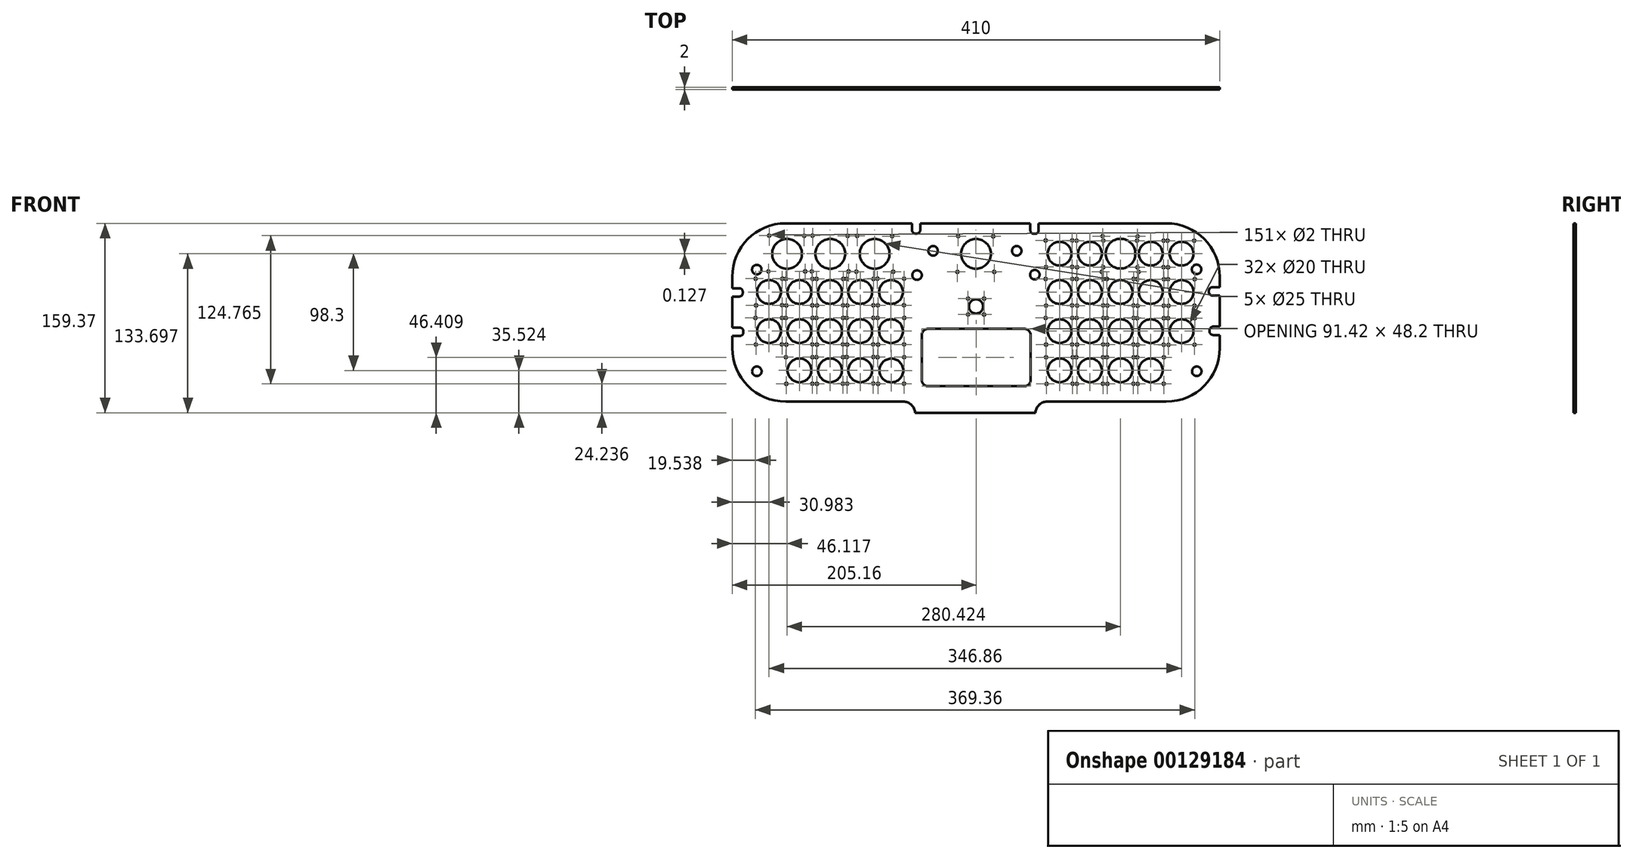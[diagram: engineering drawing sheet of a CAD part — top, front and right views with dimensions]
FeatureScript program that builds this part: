
annotation { "Feature Type Name" : "Feature", "Feature Type Description" : "" }
export const myFeature = defineFeature(function(context is Context, id is Id, definition is map)
    precondition{}
    {
        {
            var Q0;
            Q0=qCreatedBy(makeId("Front.planeOp"),FACE);
            var sketch = newSketch(context, id + "F0", { "sketchPlane" : qUnion([Q0])});
            skLineSegment(sketch, "E0.bottom", {"start": v(205, -75) * mm, "end": v(-205, -75) * mm});
            skLineSegment(sketch, "E0.top", {"start": v(205, 75) * mm, "end": v(-205, 75) * mm});
            skLineSegment(sketch, "E0.left", {"start": v(205, -75) * mm, "end": v(205, 75) * mm});
            skLineSegment(sketch, "E0.right", {"start": v(-205, -75) * mm, "end": v(-205, 75) * mm});
            skSolve(sketch);
        }
        {
            var Q0;
            Q0=qSketchRegion(id+"F0",true);
            extrude(context, id + "F1", {"entities" : qUnion([Q0]), "depth" : 1 * mm, "hasSecondDirection" : true, "secondDirectionOppositeDirection" : true, "secondDirectionDepth" : 1 * mm});
        }
        {
            var Q0;
            Q0=makeQuery(id+"F1.opExtrude","SWEPT_EDGE",EDGE,{"disambiguationData":[OSD([sQuery(id+"F0.wireOp",EDGE,"E0.top"),sQuery(id+"F0.wireOp",EDGE,"E0.right")])]});
            var Q1;
            Q1=makeQuery(id+"F1.opExtrude","SWEPT_EDGE",EDGE,{"disambiguationData":[OSD([sQuery(id+"F0.wireOp",EDGE,"E0.bottom"),sQuery(id+"F0.wireOp",EDGE,"E0.right")])]});
            fillet(context, id + "F2", {"entities" : qUnion([Q0, Q1]), "radius" : 45 * mm, "tangentPropagation" : true, "allowEdgeOverflow" : false});
        }
        {
            var Q0;
            Q0=makeQuery(id+"F1.opExtrude","SWEPT_EDGE",EDGE,{"disambiguationData":[OSD([sQuery(id+"F0.wireOp",EDGE,"E0.top"),sQuery(id+"F0.wireOp",EDGE,"E0.left")])]});
            fillet(context, id + "F3", {"entities" : qUnion([Q0]), "radius" : 45 * mm, "tangentPropagation" : true, "allowEdgeOverflow" : false});
        }
        {
            var Q0;
            Q0=makeQuery(id+"F1.opExtrude","SWEPT_EDGE",EDGE,{"disambiguationData":[OSD([sQuery(id+"F0.wireOp",EDGE,"E0.bottom"),sQuery(id+"F0.wireOp",EDGE,"E0.left")])]});
            fillet(context, id + "F4", {"entities" : qUnion([Q0]), "radius" : 45 * mm, "tangentPropagation" : true, "allowEdgeOverflow" : false});
        }
        {
            var Q0;
            Q0=qCreatedBy(makeId("Front.planeOp"),FACE);
            var sketch = newSketch(context, id + "F5", { "sketchPlane" : qUnion([Q0])});
            skLineSegment(sketch, "E1.bottom", {"start": v(-51.28, -63.48) * mm, "end": v(50, -63.48) * mm});
            skLineSegment(sketch, "E1.top", {"start": v(-51.28, -84.37) * mm, "end": v(50, -84.37) * mm});
            skLineSegment(sketch, "E1.left", {"start": v(-51.28, -63.48) * mm, "end": v(-51.28, -84.37) * mm});
            skLineSegment(sketch, "E1.right", {"start": v(50, -63.48) * mm, "end": v(50, -84.37) * mm});
            skSolve(sketch);
        }
        {
            var Q0;
            Q0=qSketchRegion(id+"F5",true);
            extrude(context, id + "F6", {"entities" : qUnion([Q0]), "operationType" : NewBodyOperationType.ADD, "depth" : 1 * mm, "hasSecondDirection" : true, "secondDirectionOppositeDirection" : true, "secondDirectionDepth" : 1 * mm});
        }
        {
            var Q0;
            Q0=makeQuery(id+"F6.boolean.opBoolean","INTERSECT",EDGE,{"derivedFrom":[makeQuery(id+"F1.opExtrude","SWEPT_FACE",FACE,{"disambiguationData":[OSD([sQuery(id+"F0.wireOp",EDGE,"E0.bottom")])]}),makeQuery(id+"F6.opExtrude","SWEPT_FACE",FACE,{"disambiguationData":[OSD([sQuery(id+"F5.wireOp",EDGE,"E1.left")])]})]});
            fillet(context, id + "F7", {"entities" : qUnion([Q0]), "radius" : 10 * mm, "tangentPropagation" : true, "allowEdgeOverflow" : false});
        }
        {
            var Q0;
            Q0=makeQuery(id+"F6.boolean.opBoolean","INTERSECT",EDGE,{"derivedFrom":[makeQuery(id+"F1.opExtrude","SWEPT_FACE",FACE,{"disambiguationData":[OSD([sQuery(id+"F0.wireOp",EDGE,"E0.bottom")])]}),makeQuery(id+"F6.opExtrude","SWEPT_FACE",FACE,{"disambiguationData":[OSD([sQuery(id+"F5.wireOp",EDGE,"E1.right")])]})]});
            fillet(context, id + "F8", {"entities" : qUnion([Q0]), "radius" : 10 * mm, "tangentPropagation" : true, "allowEdgeOverflow" : false});
        }
        {
            var Q0;
            Q0=qCreatedBy(makeId("Front.planeOp"),FACE);
            var sketch = newSketch(context, id + "F9", { "sketchPlane" : qUnion([Q0])});
            skCircle(sketch, "E2", {"center": v(0, 49.33) * mm, "radius": 12.5 * mm});
            skCircle(sketch, "E3", {"center": v(0, 5.03) * mm, "radius": 6 * mm});
            skCircle(sketch, "E4", {"center": v(-158.88, 49.33) * mm, "radius": 12.5 * mm});
            skCircle(sketch, "E5", {"center": v(-122.54, 49.33) * mm, "radius": 12.5 * mm});
            skCircle(sketch, "E6", {"center": v(-85.24, 49.33) * mm, "radius": 12.5 * mm});
            skCircle(sketch, "E7", {"center": v(172.84, 17.2) * mm, "radius": 10 * mm});
            skCircle(sketch, "E8", {"center": v(172.84, -15.76) * mm, "radius": 10 * mm});
            skCircle(sketch, "E9", {"center": v(146.94, -48.73) * mm, "radius": 10 * mm});
            skCircle(sketch, "E10", {"center": v(146.94, 17.2) * mm, "radius": 10 * mm});
            skCircle(sketch, "E11", {"center": v(146.94, -15.76) * mm, "radius": 10 * mm});
            skCircle(sketch, "E12", {"center": v(121.54, -48.73) * mm, "radius": 10 * mm});
            skCircle(sketch, "E13", {"center": v(121.54, 17.2) * mm, "radius": 10 * mm});
            skCircle(sketch, "E14", {"center": v(121.54, -15.76) * mm, "radius": 10 * mm});
            skCircle(sketch, "E15", {"center": v(95.83, -48.73) * mm, "radius": 10 * mm});
            skCircle(sketch, "E16", {"center": v(95.83, 17.2) * mm, "radius": 10 * mm});
            skCircle(sketch, "E17", {"center": v(95.83, -15.76) * mm, "radius": 10 * mm});
            skCircle(sketch, "E18", {"center": v(70.27, -48.73) * mm, "radius": 10 * mm});
            skCircle(sketch, "E19", {"center": v(70.27, 17.2) * mm, "radius": 10 * mm});
            skCircle(sketch, "E20", {"center": v(70.27, -15.76) * mm, "radius": 10 * mm});
            skCircle(sketch, "E21", {"center": v(172.84, 49.45) * mm, "radius": 10 * mm});
            skCircle(sketch, "E22", {"center": v(146.94, 49.45) * mm, "radius": 10 * mm});
            skCircle(sketch, "E23", {"center": v(121.54, 49.45) * mm, "radius": 12.5 * mm});
            skCircle(sketch, "E24", {"center": v(95.83, 49.45) * mm, "radius": 10 * mm});
            skCircle(sketch, "E25", {"center": v(70.27, 49.45) * mm, "radius": 10 * mm});
            skCircle(sketch, "E26", {"center": v(-71.45, 17.2) * mm, "radius": 10 * mm});
            skCircle(sketch, "E27", {"center": v(-71.45, -15.76) * mm, "radius": 10 * mm});
            skCircle(sketch, "E28", {"center": v(-97.35, -48.73) * mm, "radius": 10 * mm});
            skCircle(sketch, "E29", {"center": v(-97.35, 17.2) * mm, "radius": 10 * mm});
            skCircle(sketch, "E30", {"center": v(-97.35, -15.76) * mm, "radius": 10 * mm});
            skCircle(sketch, "E31", {"center": v(-122.75, -48.73) * mm, "radius": 10 * mm});
            skCircle(sketch, "E32", {"center": v(-122.75, 17.2) * mm, "radius": 10 * mm});
            skCircle(sketch, "E33", {"center": v(-122.75, -15.76) * mm, "radius": 10 * mm});
            skCircle(sketch, "E34", {"center": v(-148.46, -48.73) * mm, "radius": 10 * mm});
            skCircle(sketch, "E35", {"center": v(-148.46, 17.2) * mm, "radius": 10 * mm});
            skCircle(sketch, "E36", {"center": v(-148.46, -15.76) * mm, "radius": 10 * mm});
            skCircle(sketch, "E37", {"center": v(-174.02, 17.2) * mm, "radius": 10 * mm});
            skCircle(sketch, "E38", {"center": v(-174.02, -15.76) * mm, "radius": 10 * mm});
            skCircle(sketch, "E39", {"center": v(-71.2, -48.85) * mm, "radius": 10 * mm});
            skLineSegment(sketch, "E40.bottom", {"start": v(-45.55, -13.86) * mm, "end": v(45.87, -13.86) * mm});
            skLineSegment(sketch, "E40.top", {"start": v(-45.55, -62.06) * mm, "end": v(45.87, -62.06) * mm});
            skLineSegment(sketch, "E40.left", {"start": v(-45.55, -13.86) * mm, "end": v(-45.55, -62.06) * mm});
            skLineSegment(sketch, "E40.right", {"start": v(45.87, -13.86) * mm, "end": v(45.87, -62.06) * mm});
            skSolve(sketch);
        }
        {
            var Q0;
            Q0=makeQuery(id+"F6.boolean.opBoolean","MERGE",FACE,{"derivedFrom":[makeQuery(id+"F1.opExtrude","CAP_FACE",FACE,{"disambiguationData":[OSD([sQuery(id+"F0.wireOp",EDGE,"E0.bottom"),sQuery(id+"F0.wireOp",EDGE,"E0.top"),sQuery(id+"F0.wireOp",EDGE,"E0.left"),sQuery(id+"F0.wireOp",EDGE,"E0.right")])],"isStart":false}),makeQuery(id+"F6.opExtrude","CAP_FACE",FACE,{"disambiguationData":[OSD([sQuery(id+"F5.wireOp",EDGE,"E1.bottom"),sQuery(id+"F5.wireOp",EDGE,"E1.top"),sQuery(id+"F5.wireOp",EDGE,"E1.left"),sQuery(id+"F5.wireOp",EDGE,"E1.right")])],"isStart":false})]});
            cPlane(context, id + "F10", {"entities" : qUnion([Q0]), "cplaneType" : CPlaneType.OFFSET, "offset" : 0 * mm, "width" : 150 * mm, "height" : 150 * mm});
        }
        {
            var Q0;
            Q0=qCreatedBy(id+"F10.planeOp",FACE);
            var sketch = newSketch(context, id + "F11", { "sketchPlane" : qUnion([Q0])});
            skLineSegment(sketch, "E41.bottom", {"start": v(-210.38, 20.36) * mm, "end": v(-199.13, 20.36) * mm});
            skLineSegment(sketch, "E41.top", {"start": v(-210.38, 13.36) * mm, "end": v(-199.13, 13.36) * mm});
            skLineSegment(sketch, "E41.left", {"start": v(-213.38, 17.36) * mm, "end": v(-213.38, 16.36) * mm});
            skLineSegment(sketch, "E41.right", {"start": v(-196.13, 17.36) * mm, "end": v(-196.13, 16.36) * mm});
            skPoint(sketch, "E42.visualSharp", {"position": v(-196.13, 20.36) * mm});
            skArc(sketch, "E42.filletArc", {"start": v(-196.13, 17.36) * mm, "mid": v(-197.01, 19.48) * mm, "end": v(-199.13, 20.36) * mm});
            skPoint(sketch, "E43.visualSharp", {"position": v(-196.13, 13.36) * mm});
            skArc(sketch, "E43.filletArc", {"start": v(-199.13, 13.36) * mm, "mid": v(-197.01, 14.23) * mm, "end": v(-196.13, 16.36) * mm});
            skPoint(sketch, "E44.visualSharp", {"position": v(-213.38, 20.36) * mm});
            skArc(sketch, "E44.filletArc", {"start": v(-210.38, 20.36) * mm, "mid": v(-212.5, 19.48) * mm, "end": v(-213.38, 17.36) * mm});
            skPoint(sketch, "E45.visualSharp", {"position": v(-213.38, 13.36) * mm});
            skArc(sketch, "E45.filletArc", {"start": v(-213.38, 16.36) * mm, "mid": v(-212.5, 14.23) * mm, "end": v(-210.38, 13.36) * mm});
            skLineSegment(sketch, "E46.bottom", {"start": v(-209.84, -12.8) * mm, "end": v(-198.59, -12.8) * mm});
            skLineSegment(sketch, "E46.top", {"start": v(-209.84, -19.8) * mm, "end": v(-198.59, -19.8) * mm});
            skLineSegment(sketch, "E46.left", {"start": v(-212.84, -15.8) * mm, "end": v(-212.84, -16.8) * mm});
            skLineSegment(sketch, "E46.right", {"start": v(-195.59, -15.8) * mm, "end": v(-195.59, -16.8) * mm});
            skPoint(sketch, "E47.visualSharp", {"position": v(-195.59, -12.8) * mm});
            skArc(sketch, "E47.filletArc", {"start": v(-195.59, -15.8) * mm, "mid": v(-196.47, -13.69) * mm, "end": v(-198.59, -12.8) * mm});
            skPoint(sketch, "E48.visualSharp", {"position": v(-195.59, -19.8) * mm});
            skArc(sketch, "E48.filletArc", {"start": v(-198.59, -19.8) * mm, "mid": v(-196.47, -18.93) * mm, "end": v(-195.59, -16.8) * mm});
            skPoint(sketch, "E49.visualSharp", {"position": v(-212.84, -12.8) * mm});
            skArc(sketch, "E49.filletArc", {"start": v(-209.84, -12.8) * mm, "mid": v(-211.96, -13.69) * mm, "end": v(-212.84, -15.8) * mm});
            skPoint(sketch, "E50.visualSharp", {"position": v(-212.84, -19.8) * mm});
            skArc(sketch, "E50.filletArc", {"start": v(-212.84, -16.8) * mm, "mid": v(-211.96, -18.93) * mm, "end": v(-209.84, -19.8) * mm});
            skLineSegment(sketch, "E51.bottom", {"start": v(198.82, 21.2) * mm, "end": v(210.07, 21.2) * mm});
            skLineSegment(sketch, "E51.top", {"start": v(198.82, 14.2) * mm, "end": v(210.07, 14.2) * mm});
            skLineSegment(sketch, "E51.left", {"start": v(195.82, 18.2) * mm, "end": v(195.82, 17.2) * mm});
            skLineSegment(sketch, "E51.right", {"start": v(213.07, 18.2) * mm, "end": v(213.07, 17.2) * mm});
            skPoint(sketch, "E52.visualSharp", {"position": v(213.07, 21.2) * mm});
            skArc(sketch, "E52.filletArc", {"start": v(213.07, 18.2) * mm, "mid": v(212.2, 20.32) * mm, "end": v(210.07, 21.2) * mm});
            skPoint(sketch, "E53.visualSharp", {"position": v(213.07, 14.2) * mm});
            skArc(sketch, "E53.filletArc", {"start": v(210.07, 14.2) * mm, "mid": v(212.2, 15.07) * mm, "end": v(213.07, 17.2) * mm});
            skPoint(sketch, "E54.visualSharp", {"position": v(195.82, 21.2) * mm});
            skArc(sketch, "E54.filletArc", {"start": v(198.82, 21.2) * mm, "mid": v(196.7, 20.32) * mm, "end": v(195.82, 18.2) * mm});
            skPoint(sketch, "E55.visualSharp", {"position": v(195.82, 14.2) * mm});
            skArc(sketch, "E55.filletArc", {"start": v(195.82, 17.2) * mm, "mid": v(196.7, 15.07) * mm, "end": v(198.82, 14.2) * mm});
            skLineSegment(sketch, "E56.bottom", {"start": v(199.36, -11.97) * mm, "end": v(210.61, -11.97) * mm});
            skLineSegment(sketch, "E56.top", {"start": v(199.36, -18.97) * mm, "end": v(210.61, -18.97) * mm});
            skLineSegment(sketch, "E56.left", {"start": v(196.36, -14.97) * mm, "end": v(196.36, -15.97) * mm});
            skLineSegment(sketch, "E56.right", {"start": v(213.61, -14.97) * mm, "end": v(213.61, -15.97) * mm});
            skPoint(sketch, "E57.visualSharp", {"position": v(213.61, -11.97) * mm});
            skArc(sketch, "E57.filletArc", {"start": v(213.61, -14.97) * mm, "mid": v(212.73, -12.85) * mm, "end": v(210.61, -11.97) * mm});
            skPoint(sketch, "E58.visualSharp", {"position": v(213.61, -18.97) * mm});
            skArc(sketch, "E58.filletArc", {"start": v(210.61, -18.97) * mm, "mid": v(212.73, -18.1) * mm, "end": v(213.61, -15.97) * mm});
            skPoint(sketch, "E59.visualSharp", {"position": v(196.36, -11.97) * mm});
            skArc(sketch, "E59.filletArc", {"start": v(199.36, -11.97) * mm, "mid": v(197.24, -12.85) * mm, "end": v(196.36, -14.97) * mm});
            skPoint(sketch, "E60.visualSharp", {"position": v(196.36, -18.97) * mm});
            skArc(sketch, "E60.filletArc", {"start": v(196.36, -15.97) * mm, "mid": v(197.24, -18.1) * mm, "end": v(199.36, -18.97) * mm});
            skLineSegment(sketch, "E61.bottom", {"start": v(-50.84, 85.12) * mm, "end": v(-49.84, 85.12) * mm});
            skLineSegment(sketch, "E61.top", {"start": v(-50.84, 66.34) * mm, "end": v(-49.84, 66.34) * mm});
            skLineSegment(sketch, "E61.left", {"start": v(-53.84, 82.12) * mm, "end": v(-53.84, 69.34) * mm});
            skLineSegment(sketch, "E61.right", {"start": v(-46.84, 82.12) * mm, "end": v(-46.84, 69.34) * mm});
            skPoint(sketch, "E62.visualSharp", {"position": v(-53.84, 85.12) * mm});
            skArc(sketch, "E62.filletArc", {"start": v(-50.84, 85.12) * mm, "mid": v(-52.96, 84.24) * mm, "end": v(-53.84, 82.12) * mm});
            skPoint(sketch, "E63.visualSharp", {"position": v(-46.84, 85.12) * mm});
            skArc(sketch, "E63.filletArc", {"start": v(-46.84, 82.12) * mm, "mid": v(-47.72, 84.24) * mm, "end": v(-49.84, 85.12) * mm});
            skPoint(sketch, "E64.visualSharp", {"position": v(-46.84, 66.34) * mm});
            skArc(sketch, "E64.filletArc", {"start": v(-49.84, 66.34) * mm, "mid": v(-47.72, 67.22) * mm, "end": v(-46.84, 69.34) * mm});
            skPoint(sketch, "E65.visualSharp", {"position": v(-53.84, 66.34) * mm});
            skArc(sketch, "E65.filletArc", {"start": v(-53.84, 69.34) * mm, "mid": v(-52.96, 67.22) * mm, "end": v(-50.84, 66.34) * mm});
            skLineSegment(sketch, "E66.bottom", {"start": v(48.7, 84.97) * mm, "end": v(49.7, 84.97) * mm});
            skLineSegment(sketch, "E66.top", {"start": v(48.7, 66.19) * mm, "end": v(49.7, 66.19) * mm});
            skLineSegment(sketch, "E66.left", {"start": v(45.7, 81.97) * mm, "end": v(45.7, 69.19) * mm});
            skLineSegment(sketch, "E66.right", {"start": v(52.7, 81.97) * mm, "end": v(52.7, 69.19) * mm});
            skPoint(sketch, "E67.visualSharp", {"position": v(45.7, 84.97) * mm});
            skArc(sketch, "E67.filletArc", {"start": v(48.7, 84.97) * mm, "mid": v(46.57, 84.09) * mm, "end": v(45.7, 81.97) * mm});
            skPoint(sketch, "E68.visualSharp", {"position": v(52.7, 84.97) * mm});
            skArc(sketch, "E68.filletArc", {"start": v(52.7, 81.97) * mm, "mid": v(51.81, 84.09) * mm, "end": v(49.7, 84.97) * mm});
            skPoint(sketch, "E69.visualSharp", {"position": v(52.7, 66.19) * mm});
            skArc(sketch, "E69.filletArc", {"start": v(49.7, 66.19) * mm, "mid": v(51.81, 67.07) * mm, "end": v(52.7, 69.19) * mm});
            skPoint(sketch, "E70.visualSharp", {"position": v(45.7, 66.19) * mm});
            skArc(sketch, "E70.filletArc", {"start": v(45.7, 69.19) * mm, "mid": v(46.57, 67.07) * mm, "end": v(48.7, 66.19) * mm});
            skSolve(sketch);
        }
        {
            var Q0;
            Q0=makeQuery(id+"F6.boolean.opBoolean","MERGE",FACE,{"derivedFrom":[makeQuery(id+"F1.opExtrude","CAP_FACE",FACE,{"disambiguationData":[OSD([sQuery(id+"F0.wireOp",EDGE,"E0.bottom"),sQuery(id+"F0.wireOp",EDGE,"E0.top"),sQuery(id+"F0.wireOp",EDGE,"E0.left"),sQuery(id+"F0.wireOp",EDGE,"E0.right")])],"isStart":false}),makeQuery(id+"F6.opExtrude","CAP_FACE",FACE,{"disambiguationData":[OSD([sQuery(id+"F5.wireOp",EDGE,"E1.bottom"),sQuery(id+"F5.wireOp",EDGE,"E1.top"),sQuery(id+"F5.wireOp",EDGE,"E1.left"),sQuery(id+"F5.wireOp",EDGE,"E1.right")])],"isStart":false})]});
            cPlane(context, id + "F12", {"entities" : qUnion([Q0]), "cplaneType" : CPlaneType.OFFSET, "offset" : 2 * mm, "oppositeDirection" : true, "width" : 150 * mm, "height" : 150 * mm});
        }
        {
            var Q0;
            Q0=qCreatedBy(id+"F12.planeOp",FACE);
            var sketch = newSketch(context, id + "F13", { "sketchPlane" : qUnion([Q0])});
            skCircle(sketch, "E71", {"center": v(-184.3, 36.01) * mm, "radius": 4 * mm});
            skCircle(sketch, "E72", {"center": v(-184.28, -49.46) * mm, "radius": 4 * mm});
            skCircle(sketch, "E73", {"center": v(-36.07, 51.83) * mm, "radius": 4 * mm});
            skCircle(sketch, "E74", {"center": v(-49.57, 31.39) * mm, "radius": 4 * mm});
            skCircle(sketch, "E75", {"center": v(34.27, 51.83) * mm, "radius": 4 * mm});
            skCircle(sketch, "E76", {"center": v(49.46, 31.76) * mm, "radius": 4 * mm});
            skCircle(sketch, "E77", {"center": v(185.45, 36.26) * mm, "radius": 4 * mm});
            skCircle(sketch, "E78", {"center": v(185.64, -49.46) * mm, "radius": 4 * mm});
            skSolve(sketch);
        }
        {
            var Q0;
            Q0=qSketchRegion(id+"F13",true);
            extrude(context, id + "F14", {"entities" : qUnion([Q0]), "operationType" : NewBodyOperationType.REMOVE, "depth" : 28.49 * mm, "hasSecondDirection" : true, "secondDirectionOppositeDirection" : true, "secondDirectionDepth" : 25 * mm});
        }
        {
            var Q0;
            Q0 = qSketchRegion(id + "F9", true);
            extrude(context, id + "F15", {"entities" : qUnion([Q0]), "operationType" : NewBodyOperationType.REMOVE, "depth" : 25 * mm, "hasSecondDirection" : true, "secondDirectionOppositeDirection" : true, "secondDirectionDepth" : 25 * mm});
        }
        {
            var Q0;
            Q0 = qSketchRegion(id + "F11", true);
            extrude(context, id + "F16", {"entities" : qUnion([Q0]), "operationType" : NewBodyOperationType.REMOVE, "oppositeDirection" : true, "depth" : 50 * mm, "hasSecondDirection" : true, "secondDirectionOppositeDirection" : false, "secondDirectionDepth" : 50 * mm});
        }
        {
            var Q0;
            Q0=makeQuery(id+"F6.boolean.opBoolean","MERGE",FACE,{"derivedFrom":[makeQuery(id+"F1.opExtrude","CAP_FACE",FACE,{"disambiguationData":[OSD([sQuery(id+"F0.wireOp",EDGE,"E0.bottom"),sQuery(id+"F0.wireOp",EDGE,"E0.top"),sQuery(id+"F0.wireOp",EDGE,"E0.left"),sQuery(id+"F0.wireOp",EDGE,"E0.right")])],"isStart":true}),makeQuery(id+"F6.opExtrude","CAP_FACE",FACE,{"disambiguationData":[OSD([sQuery(id+"F5.wireOp",EDGE,"E1.bottom"),sQuery(id+"F5.wireOp",EDGE,"E1.top"),sQuery(id+"F5.wireOp",EDGE,"E1.left"),sQuery(id+"F5.wireOp",EDGE,"E1.right")])],"isStart":true})]});
            cPlane(context, id + "F17", {"entities" : qUnion([Q0]), "cplaneType" : CPlaneType.OFFSET, "offset" : 0 * mm, "oppositeDirection" : true, "width" : 150 * mm, "height" : 150 * mm});
        }
        {
            var Q0;
            Q0=qCreatedBy(id+"F17.planeOp",FACE);
            var sketch = newSketch(context, id + "F18", { "sketchPlane" : qUnion([Q0])});
            skLineSegment(sketch, "E79.bottom", {"start": v(184.07, 27.38) * mm, "end": v(163.8, 27.38) * mm, "construction": true});
            skLineSegment(sketch, "E79.top", {"start": v(184.07, 7.22) * mm, "end": v(163.8, 7.22) * mm, "construction": true});
            skLineSegment(sketch, "E79.left", {"start": v(184.07, 27.38) * mm, "end": v(184.07, 7.22) * mm, "construction": true});
            skLineSegment(sketch, "E79.right", {"start": v(163.8, 27.38) * mm, "end": v(163.8, 7.22) * mm, "construction": true});
            skPoint(sketch, "E80", {"position": v(185.32, 28.38) * mm});
            skPoint(sketch, "E81", {"position": v(162.91, 28.38) * mm});
            skPoint(sketch, "E82", {"position": v(184.95, 5.97) * mm});
            skPoint(sketch, "E83", {"position": v(163.04, 6.1) * mm});
            skLineSegment(sketch, "E84.bottom", {"start": v(158.64, 27.26) * mm, "end": v(138.36, 27.26) * mm, "construction": true});
            skLineSegment(sketch, "E84.top", {"start": v(158.64, 7.1) * mm, "end": v(138.36, 7.1) * mm, "construction": true});
            skLineSegment(sketch, "E84.left", {"start": v(158.64, 27.26) * mm, "end": v(158.64, 7.1) * mm, "construction": true});
            skLineSegment(sketch, "E84.right", {"start": v(138.36, 27.26) * mm, "end": v(138.36, 7.1) * mm, "construction": true});
            skPoint(sketch, "E85", {"position": v(159.89, 28.26) * mm});
            skPoint(sketch, "E86", {"position": v(137.48, 28.26) * mm});
            skPoint(sketch, "E87", {"position": v(159.51, 5.85) * mm});
            skPoint(sketch, "E88", {"position": v(137.6, 5.98) * mm});
            skLineSegment(sketch, "E89.bottom", {"start": v(132.78, 27.26) * mm, "end": v(112.5, 27.26) * mm, "construction": true});
            skLineSegment(sketch, "E89.top", {"start": v(132.78, 7.1) * mm, "end": v(112.5, 7.1) * mm, "construction": true});
            skLineSegment(sketch, "E89.left", {"start": v(132.78, 27.26) * mm, "end": v(132.78, 7.1) * mm, "construction": true});
            skLineSegment(sketch, "E89.right", {"start": v(112.5, 27.26) * mm, "end": v(112.5, 7.1) * mm, "construction": true});
            skPoint(sketch, "E90", {"position": v(134.03, 28.26) * mm});
            skPoint(sketch, "E91", {"position": v(111.62, 28.26) * mm});
            skPoint(sketch, "E92", {"position": v(133.66, 5.85) * mm});
            skPoint(sketch, "E93", {"position": v(111.75, 5.98) * mm});
            skLineSegment(sketch, "E94.bottom", {"start": v(107.35, 27.26) * mm, "end": v(87.07, 27.26) * mm, "construction": true});
            skLineSegment(sketch, "E94.top", {"start": v(107.35, 7.1) * mm, "end": v(87.07, 7.1) * mm, "construction": true});
            skLineSegment(sketch, "E94.left", {"start": v(107.35, 27.26) * mm, "end": v(107.35, 7.1) * mm, "construction": true});
            skLineSegment(sketch, "E94.right", {"start": v(87.07, 27.26) * mm, "end": v(87.07, 7.1) * mm, "construction": true});
            skPoint(sketch, "E95", {"position": v(108.6, 28.26) * mm});
            skPoint(sketch, "E96", {"position": v(86.19, 28.26) * mm});
            skPoint(sketch, "E97", {"position": v(108.22, 5.85) * mm});
            skPoint(sketch, "E98", {"position": v(86.31, 5.98) * mm});
            skLineSegment(sketch, "E99.bottom", {"start": v(81.63, 27.4) * mm, "end": v(61.35, 27.4) * mm, "construction": true});
            skLineSegment(sketch, "E99.top", {"start": v(81.63, 7.24) * mm, "end": v(61.35, 7.24) * mm, "construction": true});
            skLineSegment(sketch, "E99.left", {"start": v(81.63, 27.4) * mm, "end": v(81.63, 7.24) * mm, "construction": true});
            skLineSegment(sketch, "E99.right", {"start": v(61.35, 27.4) * mm, "end": v(61.35, 7.24) * mm, "construction": true});
            skPoint(sketch, "E100", {"position": v(82.88, 28.4) * mm});
            skPoint(sketch, "E101", {"position": v(60.47, 28.4) * mm});
            skPoint(sketch, "E102", {"position": v(82.5, 6) * mm});
            skPoint(sketch, "E103", {"position": v(60.6, 6.12) * mm});
            skLineSegment(sketch, "E104.bottom", {"start": v(184.21, -5.62) * mm, "end": v(163.93, -5.62) * mm, "construction": true});
            skLineSegment(sketch, "E104.top", {"start": v(184.21, -25.78) * mm, "end": v(163.93, -25.78) * mm, "construction": true});
            skLineSegment(sketch, "E104.left", {"start": v(184.21, -5.62) * mm, "end": v(184.21, -25.78) * mm, "construction": true});
            skLineSegment(sketch, "E104.right", {"start": v(163.93, -5.62) * mm, "end": v(163.93, -25.78) * mm, "construction": true});
            skPoint(sketch, "E105", {"position": v(185.46, -4.62) * mm});
            skPoint(sketch, "E106", {"position": v(163.05, -4.62) * mm});
            skPoint(sketch, "E107", {"position": v(185.09, -27.03) * mm});
            skPoint(sketch, "E108", {"position": v(163.18, -26.9) * mm});
            skLineSegment(sketch, "E109.bottom", {"start": v(158.64, -5.62) * mm, "end": v(138.36, -5.62) * mm, "construction": true});
            skLineSegment(sketch, "E109.top", {"start": v(158.64, -25.78) * mm, "end": v(138.36, -25.78) * mm, "construction": true});
            skLineSegment(sketch, "E109.left", {"start": v(158.64, -5.62) * mm, "end": v(158.64, -25.78) * mm, "construction": true});
            skLineSegment(sketch, "E109.right", {"start": v(138.36, -5.62) * mm, "end": v(138.36, -25.78) * mm, "construction": true});
            skPoint(sketch, "E110", {"position": v(159.89, -4.62) * mm});
            skPoint(sketch, "E111", {"position": v(137.48, -4.62) * mm});
            skPoint(sketch, "E112", {"position": v(159.51, -27.03) * mm});
            skPoint(sketch, "E113", {"position": v(137.6, -26.9) * mm});
            skLineSegment(sketch, "E114.bottom", {"start": v(132.92, -5.62) * mm, "end": v(112.64, -5.62) * mm, "construction": true});
            skLineSegment(sketch, "E114.top", {"start": v(132.92, -25.78) * mm, "end": v(112.64, -25.78) * mm, "construction": true});
            skLineSegment(sketch, "E114.left", {"start": v(132.92, -5.62) * mm, "end": v(132.92, -25.78) * mm, "construction": true});
            skLineSegment(sketch, "E114.right", {"start": v(112.64, -5.62) * mm, "end": v(112.64, -25.78) * mm, "construction": true});
            skPoint(sketch, "E115", {"position": v(134.17, -4.62) * mm});
            skPoint(sketch, "E116", {"position": v(111.76, -4.62) * mm});
            skPoint(sketch, "E117", {"position": v(133.8, -27.03) * mm});
            skPoint(sketch, "E118", {"position": v(111.89, -26.9) * mm});
            skLineSegment(sketch, "E119.bottom", {"start": v(107.49, -5.62) * mm, "end": v(87.2, -5.62) * mm, "construction": true});
            skLineSegment(sketch, "E119.top", {"start": v(107.49, -25.78) * mm, "end": v(87.2, -25.78) * mm, "construction": true});
            skLineSegment(sketch, "E119.left", {"start": v(107.49, -5.62) * mm, "end": v(107.49, -25.78) * mm, "construction": true});
            skLineSegment(sketch, "E119.right", {"start": v(87.2, -5.62) * mm, "end": v(87.2, -25.78) * mm, "construction": true});
            skPoint(sketch, "E120", {"position": v(108.74, -4.62) * mm});
            skPoint(sketch, "E121", {"position": v(86.33, -4.62) * mm});
            skPoint(sketch, "E122", {"position": v(108.36, -27.03) * mm});
            skPoint(sketch, "E123", {"position": v(86.45, -26.9) * mm});
            skLineSegment(sketch, "E124.bottom", {"start": v(81.5, -5.62) * mm, "end": v(61.2, -5.62) * mm, "construction": true});
            skLineSegment(sketch, "E124.top", {"start": v(81.5, -25.78) * mm, "end": v(61.2, -25.78) * mm, "construction": true});
            skLineSegment(sketch, "E124.left", {"start": v(81.5, -5.62) * mm, "end": v(81.5, -25.78) * mm, "construction": true});
            skLineSegment(sketch, "E124.right", {"start": v(61.2, -5.62) * mm, "end": v(61.2, -25.78) * mm, "construction": true});
            skPoint(sketch, "E125", {"position": v(82.74, -4.62) * mm});
            skPoint(sketch, "E126", {"position": v(60.33, -4.62) * mm});
            skPoint(sketch, "E127", {"position": v(82.37, -27.03) * mm});
            skPoint(sketch, "E128", {"position": v(60.46, -26.9) * mm});
            skLineSegment(sketch, "E129.bottom", {"start": v(158.65, -38.7) * mm, "end": v(138.37, -38.7) * mm, "construction": true});
            skLineSegment(sketch, "E129.top", {"start": v(158.65, -58.85) * mm, "end": v(138.37, -58.85) * mm, "construction": true});
            skLineSegment(sketch, "E129.left", {"start": v(158.65, -38.7) * mm, "end": v(158.65, -58.85) * mm, "construction": true});
            skLineSegment(sketch, "E129.right", {"start": v(138.37, -38.7) * mm, "end": v(138.37, -58.85) * mm, "construction": true});
            skPoint(sketch, "E130", {"position": v(159.9, -37.69) * mm});
            skPoint(sketch, "E131", {"position": v(137.5, -37.69) * mm});
            skPoint(sketch, "E132", {"position": v(159.53, -60.1) * mm});
            skPoint(sketch, "E133", {"position": v(137.62, -59.97) * mm});
            skLineSegment(sketch, "E134.bottom", {"start": v(132.95, -38.7) * mm, "end": v(112.67, -38.7) * mm, "construction": true});
            skLineSegment(sketch, "E134.top", {"start": v(132.95, -58.85) * mm, "end": v(112.67, -58.85) * mm, "construction": true});
            skLineSegment(sketch, "E134.left", {"start": v(132.95, -38.7) * mm, "end": v(132.95, -58.85) * mm, "construction": true});
            skLineSegment(sketch, "E134.right", {"start": v(112.67, -38.7) * mm, "end": v(112.67, -58.85) * mm, "construction": true});
            skPoint(sketch, "E135", {"position": v(134.2, -37.69) * mm});
            skPoint(sketch, "E136", {"position": v(111.8, -37.69) * mm});
            skPoint(sketch, "E137", {"position": v(133.83, -60.1) * mm});
            skPoint(sketch, "E138", {"position": v(111.92, -59.97) * mm});
            skLineSegment(sketch, "E139.bottom", {"start": v(107.44, -38.5) * mm, "end": v(87.16, -38.5) * mm, "construction": true});
            skLineSegment(sketch, "E139.top", {"start": v(107.44, -58.66) * mm, "end": v(87.16, -58.66) * mm, "construction": true});
            skLineSegment(sketch, "E139.left", {"start": v(107.44, -38.5) * mm, "end": v(107.44, -58.66) * mm, "construction": true});
            skLineSegment(sketch, "E139.right", {"start": v(87.16, -38.5) * mm, "end": v(87.16, -58.66) * mm, "construction": true});
            skPoint(sketch, "E140", {"position": v(108.7, -37.5) * mm});
            skPoint(sketch, "E141", {"position": v(86.29, -37.5) * mm});
            skPoint(sketch, "E142", {"position": v(108.32, -59.91) * mm});
            skPoint(sketch, "E143", {"position": v(86.41, -59.79) * mm});
            skLineSegment(sketch, "E144.bottom", {"start": v(81.56, -38.7) * mm, "end": v(61.28, -38.7) * mm, "construction": true});
            skLineSegment(sketch, "E144.top", {"start": v(81.56, -58.85) * mm, "end": v(61.28, -58.85) * mm, "construction": true});
            skLineSegment(sketch, "E144.left", {"start": v(81.56, -38.7) * mm, "end": v(81.56, -58.85) * mm, "construction": true});
            skLineSegment(sketch, "E144.right", {"start": v(61.28, -38.7) * mm, "end": v(61.28, -58.85) * mm, "construction": true});
            skPoint(sketch, "E145", {"position": v(82.8, -37.69) * mm});
            skPoint(sketch, "E146", {"position": v(60.4, -37.69) * mm});
            skPoint(sketch, "E147", {"position": v(82.43, -60.1) * mm});
            skPoint(sketch, "E148", {"position": v(60.53, -59.97) * mm});
            skLineSegment(sketch, "E149.bottom", {"start": v(-59.78, 59.6) * mm, "end": v(-80.07, 59.6) * mm, "construction": true});
            skLineSegment(sketch, "E149.top", {"start": v(-59.78, 39.44) * mm, "end": v(-80.07, 39.44) * mm, "construction": true});
            skLineSegment(sketch, "E149.left", {"start": v(-59.78, 59.6) * mm, "end": v(-59.78, 39.44) * mm, "construction": true});
            skLineSegment(sketch, "E149.right", {"start": v(-80.07, 59.6) * mm, "end": v(-80.07, 39.44) * mm, "construction": true});
            skPoint(sketch, "E150", {"position": v(-58.53, 60.6) * mm});
            skPoint(sketch, "E151", {"position": v(-80.94, 60.6) * mm});
            skPoint(sketch, "E152", {"position": v(-58.9, 38.19) * mm});
            skPoint(sketch, "E153", {"position": v(-80.82, 38.31) * mm});
            skLineSegment(sketch, "E154.bottom", {"start": v(-85.9, 59.39) * mm, "end": v(-106.17, 59.39) * mm, "construction": true});
            skLineSegment(sketch, "E154.top", {"start": v(-85.9, 39.23) * mm, "end": v(-106.17, 39.23) * mm, "construction": true});
            skLineSegment(sketch, "E154.left", {"start": v(-85.9, 59.39) * mm, "end": v(-85.9, 39.23) * mm, "construction": true});
            skLineSegment(sketch, "E154.right", {"start": v(-106.17, 59.39) * mm, "end": v(-106.17, 39.23) * mm, "construction": true});
            skPoint(sketch, "E155", {"position": v(-84.64, 60.39) * mm});
            skPoint(sketch, "E156", {"position": v(-107.05, 60.39) * mm});
            skPoint(sketch, "E157", {"position": v(-85.02, 37.98) * mm});
            skPoint(sketch, "E158", {"position": v(-106.92, 38.1) * mm});
            skLineSegment(sketch, "E159.bottom", {"start": v(-136.63, 59.39) * mm, "end": v(-156.91, 59.39) * mm, "construction": true});
            skLineSegment(sketch, "E159.top", {"start": v(-136.63, 39.23) * mm, "end": v(-156.91, 39.23) * mm, "construction": true});
            skLineSegment(sketch, "E159.left", {"start": v(-136.63, 59.39) * mm, "end": v(-136.63, 39.23) * mm, "construction": true});
            skLineSegment(sketch, "E159.right", {"start": v(-156.91, 59.39) * mm, "end": v(-156.91, 39.23) * mm, "construction": true});
            skPoint(sketch, "E160", {"position": v(-135.38, 60.39) * mm});
            skPoint(sketch, "E161", {"position": v(-157.79, 60.39) * mm});
            skPoint(sketch, "E162", {"position": v(-135.76, 37.98) * mm});
            skPoint(sketch, "E163", {"position": v(-157.66, 38.1) * mm});
            skLineSegment(sketch, "E164.bottom", {"start": v(-162.32, 59.39) * mm, "end": v(-182.6, 59.39) * mm, "construction": true});
            skLineSegment(sketch, "E164.top", {"start": v(-162.32, 39.23) * mm, "end": v(-182.6, 39.23) * mm, "construction": true});
            skLineSegment(sketch, "E164.left", {"start": v(-162.32, 59.39) * mm, "end": v(-162.32, 39.23) * mm, "construction": true});
            skLineSegment(sketch, "E164.right", {"start": v(-182.6, 59.39) * mm, "end": v(-182.6, 39.23) * mm, "construction": true});
            skPoint(sketch, "E165", {"position": v(-161.07, 60.39) * mm});
            skPoint(sketch, "E166", {"position": v(-183.48, 60.39) * mm});
            skPoint(sketch, "E167", {"position": v(-161.44, 37.98) * mm});
            skPoint(sketch, "E168", {"position": v(-183.35, 38.1) * mm});
            skLineSegment(sketch, "E169.bottom", {"start": v(-59.78, 27.17) * mm, "end": v(-80.07, 27.17) * mm, "construction": true});
            skLineSegment(sketch, "E169.top", {"start": v(-59.78, 7.02) * mm, "end": v(-80.07, 7.02) * mm, "construction": true});
            skLineSegment(sketch, "E169.left", {"start": v(-59.78, 27.17) * mm, "end": v(-59.78, 7.02) * mm, "construction": true});
            skLineSegment(sketch, "E169.right", {"start": v(-80.07, 27.17) * mm, "end": v(-80.07, 7.02) * mm, "construction": true});
            skPoint(sketch, "E170", {"position": v(-58.53, 28.17) * mm});
            skPoint(sketch, "E171", {"position": v(-80.94, 28.17) * mm});
            skPoint(sketch, "E172", {"position": v(-58.9, 5.77) * mm});
            skPoint(sketch, "E173", {"position": v(-80.82, 5.9) * mm});
            skLineSegment(sketch, "E174.bottom", {"start": v(-85.9, 27.17) * mm, "end": v(-106.17, 27.17) * mm, "construction": true});
            skLineSegment(sketch, "E174.top", {"start": v(-85.9, 7.02) * mm, "end": v(-106.17, 7.02) * mm, "construction": true});
            skLineSegment(sketch, "E174.left", {"start": v(-85.9, 27.17) * mm, "end": v(-85.9, 7.02) * mm, "construction": true});
            skLineSegment(sketch, "E174.right", {"start": v(-106.17, 27.17) * mm, "end": v(-106.17, 7.02) * mm, "construction": true});
            skPoint(sketch, "E175", {"position": v(-84.64, 28.17) * mm});
            skPoint(sketch, "E176", {"position": v(-107.05, 28.17) * mm});
            skPoint(sketch, "E177", {"position": v(-85.02, 5.77) * mm});
            skPoint(sketch, "E178", {"position": v(-106.92, 5.9) * mm});
            skLineSegment(sketch, "E179.bottom", {"start": v(-111.37, 27.17) * mm, "end": v(-131.65, 27.17) * mm, "construction": true});
            skLineSegment(sketch, "E179.top", {"start": v(-111.37, 7.02) * mm, "end": v(-131.65, 7.02) * mm, "construction": true});
            skLineSegment(sketch, "E179.left", {"start": v(-111.37, 27.17) * mm, "end": v(-111.37, 7.02) * mm, "construction": true});
            skLineSegment(sketch, "E179.right", {"start": v(-131.65, 27.17) * mm, "end": v(-131.65, 7.02) * mm, "construction": true});
            skPoint(sketch, "E180", {"position": v(-110.12, 28.17) * mm});
            skPoint(sketch, "E181", {"position": v(-132.52, 28.17) * mm});
            skPoint(sketch, "E182", {"position": v(-110.5, 5.77) * mm});
            skPoint(sketch, "E183", {"position": v(-132.4, 5.9) * mm});
            skLineSegment(sketch, "E184.bottom", {"start": v(-136.84, 26.96) * mm, "end": v(-157.12, 26.96) * mm, "construction": true});
            skLineSegment(sketch, "E184.top", {"start": v(-136.84, 6.8) * mm, "end": v(-157.12, 6.8) * mm, "construction": true});
            skLineSegment(sketch, "E184.left", {"start": v(-136.84, 26.96) * mm, "end": v(-136.84, 6.8) * mm, "construction": true});
            skLineSegment(sketch, "E184.right", {"start": v(-157.12, 26.96) * mm, "end": v(-157.12, 6.8) * mm, "construction": true});
            skPoint(sketch, "E185", {"position": v(-135.6, 27.96) * mm});
            skPoint(sketch, "E186", {"position": v(-158, 27.96) * mm});
            skPoint(sketch, "E187", {"position": v(-135.97, 5.56) * mm});
            skPoint(sketch, "E188", {"position": v(-157.88, 5.68) * mm});
            skLineSegment(sketch, "E189.bottom", {"start": v(-162.74, 26.96) * mm, "end": v(-183.02, 26.96) * mm, "construction": true});
            skLineSegment(sketch, "E189.top", {"start": v(-162.74, 6.8) * mm, "end": v(-183.02, 6.8) * mm, "construction": true});
            skLineSegment(sketch, "E189.left", {"start": v(-162.74, 26.96) * mm, "end": v(-162.74, 6.8) * mm, "construction": true});
            skLineSegment(sketch, "E189.right", {"start": v(-183.02, 26.96) * mm, "end": v(-183.02, 6.8) * mm, "construction": true});
            skPoint(sketch, "E190", {"position": v(-161.49, 27.96) * mm});
            skPoint(sketch, "E191", {"position": v(-183.9, 27.96) * mm});
            skPoint(sketch, "E192", {"position": v(-161.86, 5.56) * mm});
            skPoint(sketch, "E193", {"position": v(-183.77, 5.68) * mm});
            skLineSegment(sketch, "E194.bottom", {"start": v(-59.78, -5.67) * mm, "end": v(-80.07, -5.67) * mm, "construction": true});
            skLineSegment(sketch, "E194.top", {"start": v(-59.78, -25.83) * mm, "end": v(-80.07, -25.83) * mm, "construction": true});
            skLineSegment(sketch, "E194.left", {"start": v(-59.78, -5.67) * mm, "end": v(-59.78, -25.83) * mm, "construction": true});
            skLineSegment(sketch, "E194.right", {"start": v(-80.07, -5.67) * mm, "end": v(-80.07, -25.83) * mm, "construction": true});
            skPoint(sketch, "E195", {"position": v(-58.53, -4.67) * mm});
            skPoint(sketch, "E196", {"position": v(-80.94, -4.67) * mm});
            skPoint(sketch, "E197", {"position": v(-58.9, -27.08) * mm});
            skPoint(sketch, "E198", {"position": v(-80.82, -26.95) * mm});
            skLineSegment(sketch, "E199.bottom", {"start": v(-85.9, -5.67) * mm, "end": v(-106.17, -5.67) * mm, "construction": true});
            skLineSegment(sketch, "E199.top", {"start": v(-85.9, -25.83) * mm, "end": v(-106.17, -25.83) * mm, "construction": true});
            skLineSegment(sketch, "E199.left", {"start": v(-85.9, -5.67) * mm, "end": v(-85.9, -25.83) * mm, "construction": true});
            skLineSegment(sketch, "E199.right", {"start": v(-106.17, -5.67) * mm, "end": v(-106.17, -25.83) * mm, "construction": true});
            skPoint(sketch, "E200", {"position": v(-84.64, -4.67) * mm});
            skPoint(sketch, "E201", {"position": v(-107.05, -4.67) * mm});
            skPoint(sketch, "E202", {"position": v(-85.02, -27.08) * mm});
            skPoint(sketch, "E203", {"position": v(-106.92, -26.95) * mm});
            skLineSegment(sketch, "E204.bottom", {"start": v(-111.37, -5.67) * mm, "end": v(-131.65, -5.67) * mm, "construction": true});
            skLineSegment(sketch, "E204.top", {"start": v(-111.37, -25.83) * mm, "end": v(-131.65, -25.83) * mm, "construction": true});
            skLineSegment(sketch, "E204.left", {"start": v(-111.37, -5.67) * mm, "end": v(-111.37, -25.83) * mm, "construction": true});
            skLineSegment(sketch, "E204.right", {"start": v(-131.65, -5.67) * mm, "end": v(-131.65, -25.83) * mm, "construction": true});
            skPoint(sketch, "E205", {"position": v(-110.12, -4.67) * mm});
            skPoint(sketch, "E206", {"position": v(-132.52, -4.67) * mm});
            skPoint(sketch, "E207", {"position": v(-110.5, -27.08) * mm});
            skPoint(sketch, "E208", {"position": v(-132.4, -26.95) * mm});
            skLineSegment(sketch, "E209.bottom", {"start": v(-136.84, -5.88) * mm, "end": v(-157.12, -5.88) * mm, "construction": true});
            skLineSegment(sketch, "E209.top", {"start": v(-136.84, -26.04) * mm, "end": v(-157.12, -26.04) * mm, "construction": true});
            skLineSegment(sketch, "E209.left", {"start": v(-136.84, -5.88) * mm, "end": v(-136.84, -26.04) * mm, "construction": true});
            skLineSegment(sketch, "E209.right", {"start": v(-157.12, -5.88) * mm, "end": v(-157.12, -26.04) * mm, "construction": true});
            skPoint(sketch, "E210", {"position": v(-135.6, -4.88) * mm});
            skPoint(sketch, "E211", {"position": v(-158, -4.88) * mm});
            skPoint(sketch, "E212", {"position": v(-135.97, -27.29) * mm});
            skPoint(sketch, "E213", {"position": v(-157.88, -27.16) * mm});
            skLineSegment(sketch, "E214.bottom", {"start": v(-162.74, -5.88) * mm, "end": v(-183.02, -5.88) * mm, "construction": true});
            skLineSegment(sketch, "E214.top", {"start": v(-162.74, -26.04) * mm, "end": v(-183.02, -26.04) * mm, "construction": true});
            skLineSegment(sketch, "E214.left", {"start": v(-162.74, -5.88) * mm, "end": v(-162.74, -26.04) * mm, "construction": true});
            skLineSegment(sketch, "E214.right", {"start": v(-183.02, -5.88) * mm, "end": v(-183.02, -26.04) * mm, "construction": true});
            skPoint(sketch, "E215", {"position": v(-161.49, -4.88) * mm});
            skPoint(sketch, "E216", {"position": v(-183.9, -4.88) * mm});
            skPoint(sketch, "E217", {"position": v(-161.86, -27.29) * mm});
            skPoint(sketch, "E218", {"position": v(-183.77, -27.16) * mm});
            skLineSegment(sketch, "E219.bottom", {"start": v(-60.2, -38.73) * mm, "end": v(-80.49, -38.73) * mm, "construction": true});
            skLineSegment(sketch, "E219.top", {"start": v(-60.2, -58.88) * mm, "end": v(-80.49, -58.88) * mm, "construction": true});
            skLineSegment(sketch, "E219.left", {"start": v(-60.2, -38.73) * mm, "end": v(-60.2, -58.88) * mm, "construction": true});
            skLineSegment(sketch, "E219.right", {"start": v(-80.49, -38.73) * mm, "end": v(-80.49, -58.88) * mm, "construction": true});
            skPoint(sketch, "E220", {"position": v(-58.95, -37.73) * mm});
            skPoint(sketch, "E221", {"position": v(-81.36, -37.73) * mm});
            skPoint(sketch, "E222", {"position": v(-59.33, -60.13) * mm});
            skPoint(sketch, "E223", {"position": v(-81.24, -60) * mm});
            skLineSegment(sketch, "E224.bottom", {"start": v(-85.68, -38.73) * mm, "end": v(-105.96, -38.73) * mm, "construction": true});
            skLineSegment(sketch, "E224.top", {"start": v(-85.68, -58.88) * mm, "end": v(-105.96, -58.88) * mm, "construction": true});
            skLineSegment(sketch, "E224.left", {"start": v(-85.68, -38.73) * mm, "end": v(-85.68, -58.88) * mm, "construction": true});
            skLineSegment(sketch, "E224.right", {"start": v(-105.96, -38.73) * mm, "end": v(-105.96, -58.88) * mm, "construction": true});
            skPoint(sketch, "E225", {"position": v(-84.43, -37.73) * mm});
            skPoint(sketch, "E226", {"position": v(-106.84, -37.73) * mm});
            skPoint(sketch, "E227", {"position": v(-84.8, -60.13) * mm});
            skPoint(sketch, "E228", {"position": v(-106.71, -60) * mm});
            skLineSegment(sketch, "E229.bottom", {"start": v(-111.37, -38.73) * mm, "end": v(-131.65, -38.73) * mm, "construction": true});
            skLineSegment(sketch, "E229.top", {"start": v(-111.37, -58.88) * mm, "end": v(-131.65, -58.88) * mm, "construction": true});
            skLineSegment(sketch, "E229.left", {"start": v(-111.37, -38.73) * mm, "end": v(-111.37, -58.88) * mm, "construction": true});
            skLineSegment(sketch, "E229.right", {"start": v(-131.65, -38.73) * mm, "end": v(-131.65, -58.88) * mm, "construction": true});
            skPoint(sketch, "E230", {"position": v(-110.12, -37.73) * mm});
            skPoint(sketch, "E231", {"position": v(-132.52, -37.73) * mm});
            skPoint(sketch, "E232", {"position": v(-110.5, -60.13) * mm});
            skPoint(sketch, "E233", {"position": v(-132.4, -60) * mm});
            skLineSegment(sketch, "E234.bottom", {"start": v(-136.84, -38.73) * mm, "end": v(-157.12, -38.73) * mm, "construction": true});
            skLineSegment(sketch, "E234.top", {"start": v(-136.84, -58.88) * mm, "end": v(-157.12, -58.88) * mm, "construction": true});
            skLineSegment(sketch, "E234.left", {"start": v(-136.84, -38.73) * mm, "end": v(-136.84, -58.88) * mm, "construction": true});
            skLineSegment(sketch, "E234.right", {"start": v(-157.12, -38.73) * mm, "end": v(-157.12, -58.88) * mm, "construction": true});
            skPoint(sketch, "E235", {"position": v(-135.6, -37.73) * mm});
            skPoint(sketch, "E236", {"position": v(-158, -37.73) * mm});
            skPoint(sketch, "E237", {"position": v(-135.97, -60.13) * mm});
            skPoint(sketch, "E238", {"position": v(-157.88, -60) * mm});
            skLineSegment(sketch, "E239.bottom", {"start": v(172.05, 62.53) * mm, "end": v(145.94, 62.53) * mm, "construction": true});
            skLineSegment(sketch, "E239.top", {"start": v(172.05, 36.42) * mm, "end": v(145.94, 36.42) * mm, "construction": true});
            skLineSegment(sketch, "E239.left", {"start": v(172.05, 62.53) * mm, "end": v(172.05, 36.42) * mm, "construction": true});
            skLineSegment(sketch, "E239.right", {"start": v(145.94, 62.53) * mm, "end": v(145.94, 36.42) * mm, "construction": true});
            skPoint(sketch, "E240", {"position": v(173.95, 64.63) * mm});
            skPoint(sketch, "E241", {"position": v(144.47, 64.42) * mm});
            skPoint(sketch, "E242", {"position": v(174.58, 34.52) * mm});
            skPoint(sketch, "E243", {"position": v(143.63, 34.52) * mm});
            skLineSegment(sketch, "E244.bottom", {"start": v(135.55, 62.5) * mm, "end": v(109.44, 62.5) * mm, "construction": true});
            skLineSegment(sketch, "E244.top", {"start": v(135.55, 36.4) * mm, "end": v(109.44, 36.4) * mm, "construction": true});
            skLineSegment(sketch, "E244.left", {"start": v(135.55, 62.5) * mm, "end": v(135.55, 36.4) * mm, "construction": true});
            skLineSegment(sketch, "E244.right", {"start": v(109.44, 62.5) * mm, "end": v(109.44, 36.4) * mm, "construction": true});
            skPoint(sketch, "E245", {"position": v(137.44, 64.6) * mm});
            skPoint(sketch, "E246", {"position": v(107.97, 64.4) * mm});
            skPoint(sketch, "E247", {"position": v(138.07, 34.5) * mm});
            skPoint(sketch, "E248", {"position": v(107.12, 34.5) * mm});
            skLineSegment(sketch, "E249.bottom", {"start": v(98.07, 62.29) * mm, "end": v(71.96, 62.29) * mm, "construction": true});
            skLineSegment(sketch, "E249.top", {"start": v(98.07, 36.18) * mm, "end": v(71.96, 36.18) * mm, "construction": true});
            skLineSegment(sketch, "E249.left", {"start": v(98.07, 62.29) * mm, "end": v(98.07, 36.18) * mm, "construction": true});
            skLineSegment(sketch, "E249.right", {"start": v(71.96, 62.29) * mm, "end": v(71.96, 36.18) * mm, "construction": true});
            skPoint(sketch, "E250", {"position": v(99.97, 64.4) * mm});
            skPoint(sketch, "E251", {"position": v(70.5, 64.18) * mm});
            skPoint(sketch, "E252", {"position": v(100.6, 34.29) * mm});
            skPoint(sketch, "E253", {"position": v(69.65, 34.29) * mm});
            skLineSegment(sketch, "E254.bottom", {"start": v(13.11, 62.1) * mm, "end": v(-13, 62.1) * mm, "construction": true});
            skLineSegment(sketch, "E254.top", {"start": v(13.11, 35.99) * mm, "end": v(-13, 35.99) * mm, "construction": true});
            skLineSegment(sketch, "E254.left", {"start": v(13.11, 62.1) * mm, "end": v(13.11, 35.99) * mm, "construction": true});
            skLineSegment(sketch, "E254.right", {"start": v(-13, 62.1) * mm, "end": v(-13, 35.99) * mm, "construction": true});
            skPoint(sketch, "E255", {"position": v(15, 64.2) * mm});
            skPoint(sketch, "E256", {"position": v(-14.47, 64) * mm});
            skPoint(sketch, "E257", {"position": v(15.64, 34.1) * mm});
            skPoint(sketch, "E258", {"position": v(-15.3, 34.1) * mm});
            skLineSegment(sketch, "E259.bottom", {"start": v(-108.3, 62.1) * mm, "end": v(-134.4, 62.1) * mm, "construction": true});
            skLineSegment(sketch, "E259.top", {"start": v(-108.3, 35.99) * mm, "end": v(-134.4, 35.99) * mm, "construction": true});
            skLineSegment(sketch, "E259.left", {"start": v(-108.3, 62.1) * mm, "end": v(-108.3, 35.99) * mm, "construction": true});
            skLineSegment(sketch, "E259.right", {"start": v(-134.4, 62.1) * mm, "end": v(-134.4, 35.99) * mm, "construction": true});
            skPoint(sketch, "E260", {"position": v(-106.4, 64.2) * mm});
            skPoint(sketch, "E261", {"position": v(-135.88, 64) * mm});
            skPoint(sketch, "E262", {"position": v(-105.77, 34.1) * mm});
            skPoint(sketch, "E263", {"position": v(-136.72, 34.1) * mm});
            skLineSegment(sketch, "E264.bottom", {"start": v(6.67, 11.63) * mm, "end": v(-6.8, 11.63) * mm, "construction": true});
            skLineSegment(sketch, "E264.top", {"start": v(6.67, -1.72) * mm, "end": v(-6.8, -1.72) * mm, "construction": true});
            skLineSegment(sketch, "E264.left", {"start": v(6.67, 11.63) * mm, "end": v(6.67, -1.72) * mm, "construction": true});
            skLineSegment(sketch, "E264.right", {"start": v(-6.8, 11.63) * mm, "end": v(-6.8, -1.72) * mm, "construction": true});
            skPoint(sketch, "E265", {"position": v(6.67, 11.63) * mm});
            skPoint(sketch, "E266", {"position": v(-6.8, 11.63) * mm});
            skPoint(sketch, "E267", {"position": v(6.67, -1.72) * mm});
            skPoint(sketch, "E268", {"position": v(-6.75, -1.78) * mm});
            skSolve(sketch);
        }
        {
            var Q0;
            Q0=sQuery(id+"F18.wireOp",VERTEX,"E240");
            var Q1;
            Q1=sQuery(id+"F18.wireOp",VERTEX,"E241");
            var Q2;
            Q2=sQuery(id+"F18.wireOp",VERTEX,"E245");
            var Q3;
            Q3=sQuery(id+"F18.wireOp",VERTEX,"E246");
            var Q4;
            Q4=sQuery(id+"F18.wireOp",VERTEX,"E250");
            var Q5;
            Q5=sQuery(id+"F18.wireOp",VERTEX,"E251");
            var Q6;
            Q6=sQuery(id+"F18.wireOp",VERTEX,"E253");
            var Q7;
            Q7=sQuery(id+"F18.wireOp",VERTEX,"E252");
            var Q8;
            Q8=sQuery(id+"F18.wireOp",VERTEX,"E248");
            var Q9;
            Q9=sQuery(id+"F18.wireOp",VERTEX,"E247");
            var Q10;
            Q10=sQuery(id+"F18.wireOp",VERTEX,"E243");
            var Q11;
            Q11=sQuery(id+"F18.wireOp",VERTEX,"E242");
            var Q12;
            Q12=sQuery(id+"F18.wireOp",VERTEX,"E80");
            var Q13;
            Q13=sQuery(id+"F18.wireOp",VERTEX,"E82");
            var Q14;
            Q14=sQuery(id+"F18.wireOp",VERTEX,"E83");
            var Q15;
            Q15=sQuery(id+"F18.wireOp",VERTEX,"E81");
            var Q16;
            Q16=sQuery(id+"F18.wireOp",VERTEX,"E85");
            var Q17;
            Q17=sQuery(id+"F18.wireOp",VERTEX,"E87");
            var Q18;
            Q18=sQuery(id+"F18.wireOp",VERTEX,"E88");
            var Q19;
            Q19=sQuery(id+"F18.wireOp",VERTEX,"E86");
            var Q20;
            Q20=sQuery(id+"F18.wireOp",VERTEX,"E90");
            var Q21;
            Q21=sQuery(id+"F18.wireOp",VERTEX,"E92");
            var Q22;
            Q22=sQuery(id+"F18.wireOp",VERTEX,"E93");
            var Q23;
            Q23=sQuery(id+"F18.wireOp",VERTEX,"E91");
            var Q24;
            Q24=sQuery(id+"F18.wireOp",VERTEX,"E95");
            var Q25;
            Q25=sQuery(id+"F18.wireOp",VERTEX,"E97");
            var Q26;
            Q26=sQuery(id+"F18.wireOp",VERTEX,"E98");
            var Q27;
            Q27=sQuery(id+"F18.wireOp",VERTEX,"E96");
            var Q28;
            Q28=sQuery(id+"F18.wireOp",VERTEX,"E100");
            var Q29;
            Q29=sQuery(id+"F18.wireOp",VERTEX,"E102");
            var Q30;
            Q30=sQuery(id+"F18.wireOp",VERTEX,"E103");
            var Q31;
            Q31=sQuery(id+"F18.wireOp",VERTEX,"E101");
            var Q32;
            Q32=sQuery(id+"F18.wireOp",VERTEX,"E105");
            var Q33;
            Q33=sQuery(id+"F18.wireOp",VERTEX,"E106");
            var Q34;
            Q34=sQuery(id+"F18.wireOp",VERTEX,"E107");
            var Q35;
            Q35=sQuery(id+"F18.wireOp",VERTEX,"E108");
            var Q36;
            Q36=sQuery(id+"F18.wireOp",VERTEX,"E112");
            var Q37;
            Q37=sQuery(id+"F18.wireOp",VERTEX,"E110");
            var Q38;
            Q38=sQuery(id+"F18.wireOp",VERTEX,"E111");
            var Q39;
            Q39=sQuery(id+"F18.wireOp",VERTEX,"E113");
            var Q40;
            Q40=sQuery(id+"F18.wireOp",VERTEX,"E115");
            var Q41;
            Q41=sQuery(id+"F18.wireOp",VERTEX,"E116");
            var Q42;
            Q42=sQuery(id+"F18.wireOp",VERTEX,"E118");
            var Q43;
            Q43=sQuery(id+"F18.wireOp",VERTEX,"E122");
            var Q44;
            Q44=sQuery(id+"F18.wireOp",VERTEX,"E120");
            var Q45;
            Q45=sQuery(id+"F18.wireOp",VERTEX,"E121");
            var Q46;
            Q46=sQuery(id+"F18.wireOp",VERTEX,"E123");
            var Q47;
            Q47=sQuery(id+"F18.wireOp",VERTEX,"E125");
            var Q48;
            Q48=sQuery(id+"F18.wireOp",VERTEX,"E127");
            var Q49;
            Q49=sQuery(id+"F18.wireOp",VERTEX,"E128");
            var Q50;
            Q50=sQuery(id+"F18.wireOp",VERTEX,"E126");
            var Q51;
            Q51=sQuery(id+"F18.wireOp",VERTEX,"E117");
            var Q52;
            Q52=makeQuery(id+"F1.opExtrude","SWEPT_BODY",BODY,{"disambiguationData":[OSD([sQuery(id+"F0.wireOp",EDGE,"E0.bottom"),sQuery(id+"F0.wireOp",EDGE,"E0.top"),sQuery(id+"F0.wireOp",EDGE,"E0.left"),sQuery(id+"F0.wireOp",EDGE,"E0.right")])]});
            hole(context, id + "F19", {"style" : HoleStyle.SIMPLE, "endStyle" : HoleEndStyle.BLIND, "holeDiameter" : 2 * mm, "holeDepth" : 20 * mm, "locations" : qUnion([Q0, Q1, Q2, Q3, Q4, Q5, Q6, Q7, Q8, Q9, Q10, Q11, Q12, Q13, Q14, Q15, Q16, Q17, Q18, Q19, Q20, Q21, Q22, Q23, Q24, Q25, Q26, Q27, Q28, Q29, Q30, Q31, Q32, Q33, Q34, Q35, Q36, Q37, Q38, Q39, Q40, Q41, Q42, Q43, Q44, Q45, Q46, Q47, Q48, Q49, Q50, Q51]), "scope" : qUnion([Q52])});
        }
        {
            var Q0;
            Q0=sQuery(id+"F18.wireOp",VERTEX,"E130");
            var Q1;
            Q1=sQuery(id+"F18.wireOp",VERTEX,"E132");
            var Q2;
            Q2=sQuery(id+"F18.wireOp",VERTEX,"E131");
            var Q3;
            Q3=sQuery(id+"F18.wireOp",VERTEX,"E133");
            var Q4;
            Q4=sQuery(id+"F18.wireOp",VERTEX,"E135");
            var Q5;
            Q5=sQuery(id+"F18.wireOp",VERTEX,"E137");
            var Q6;
            Q6=sQuery(id+"F18.wireOp",VERTEX,"E138");
            var Q7;
            Q7=sQuery(id+"F18.wireOp",VERTEX,"E136");
            var Q8;
            Q8=sQuery(id+"F18.wireOp",VERTEX,"E140");
            var Q9;
            Q9=sQuery(id+"F18.wireOp",VERTEX,"E142");
            var Q10;
            Q10=sQuery(id+"F18.wireOp",VERTEX,"E143");
            var Q11;
            Q11=sQuery(id+"F18.wireOp",VERTEX,"E141");
            var Q12;
            Q12=sQuery(id+"F18.wireOp",VERTEX,"E145");
            var Q13;
            Q13=sQuery(id+"F18.wireOp",VERTEX,"E147");
            var Q14;
            Q14=sQuery(id+"F18.wireOp",VERTEX,"E146");
            var Q15;
            Q15=sQuery(id+"F18.wireOp",VERTEX,"E148");
            var Q16;
            Q16=sQuery(id+"F18.wireOp",VERTEX,"E255");
            var Q17;
            Q17=sQuery(id+"F18.wireOp",VERTEX,"E257");
            var Q18;
            Q18=sQuery(id+"F18.wireOp",VERTEX,"E258");
            var Q19;
            Q19=sQuery(id+"F18.wireOp",VERTEX,"E256");
            var Q20;
            Q20=sQuery(id+"F18.wireOp",VERTEX,"E220");
            var Q21;
            Q21=sQuery(id+"F18.wireOp",VERTEX,"E222");
            var Q22;
            Q22=sQuery(id+"F18.wireOp",VERTEX,"E221");
            var Q23;
            Q23=sQuery(id+"F18.wireOp",VERTEX,"E223");
            var Q24;
            Q24=sQuery(id+"F18.wireOp",VERTEX,"E227");
            var Q25;
            Q25=sQuery(id+"F18.wireOp",VERTEX,"E225");
            var Q26;
            Q26=sQuery(id+"F18.wireOp",VERTEX,"E226");
            var Q27;
            Q27=sQuery(id+"F18.wireOp",VERTEX,"E228");
            var Q28;
            Q28=sQuery(id+"F18.wireOp",VERTEX,"E232");
            var Q29;
            Q29=sQuery(id+"F18.wireOp",VERTEX,"E230");
            var Q30;
            Q30=sQuery(id+"F18.wireOp",VERTEX,"E231");
            var Q31;
            Q31=sQuery(id+"F18.wireOp",VERTEX,"E233");
            var Q32;
            Q32=sQuery(id+"F18.wireOp",VERTEX,"E237");
            var Q33;
            Q33=sQuery(id+"F18.wireOp",VERTEX,"E235");
            var Q34;
            Q34=sQuery(id+"F18.wireOp",VERTEX,"E236");
            var Q35;
            Q35=sQuery(id+"F18.wireOp",VERTEX,"E238");
            var Q36;
            Q36=sQuery(id+"F18.wireOp",VERTEX,"E265");
            var Q37;
            Q37=sQuery(id+"F18.wireOp",VERTEX,"E266");
            var Q38;
            Q38=sQuery(id+"F18.wireOp",VERTEX,"E267");
            var Q39;
            Q39=sQuery(id+"F18.wireOp",VERTEX,"E268");
            var Q40;
            Q40=makeQuery(id+"F1.opExtrude","SWEPT_BODY",BODY,{"disambiguationData":[OSD([sQuery(id+"F0.wireOp",EDGE,"E0.bottom"),sQuery(id+"F0.wireOp",EDGE,"E0.top"),sQuery(id+"F0.wireOp",EDGE,"E0.left"),sQuery(id+"F0.wireOp",EDGE,"E0.right")])]});
            hole(context, id + "F20", {"style" : HoleStyle.SIMPLE, "endStyle" : HoleEndStyle.BLIND, "holeDiameter" : 2 * mm, "holeDepth" : 20 * mm, "locations" : qUnion([Q0, Q1, Q2, Q3, Q4, Q5, Q6, Q7, Q8, Q9, Q10, Q11, Q12, Q13, Q14, Q15, Q16, Q17, Q18, Q19, Q20, Q21, Q22, Q23, Q24, Q25, Q26, Q27, Q28, Q29, Q30, Q31, Q32, Q33, Q34, Q35, Q36, Q37, Q38, Q39]), "scope" : qUnion([Q40])});
        }
        {
            var Q0;
            Q0=sQuery(id+"F18.wireOp",VERTEX,"E150");
            var Q1;
            Q1=sQuery(id+"F18.wireOp",VERTEX,"E151");
            var Q2;
            Q2=sQuery(id+"F18.wireOp",VERTEX,"E152");
            var Q3;
            Q3=sQuery(id+"F18.wireOp",VERTEX,"E153");
            var Q4;
            Q4=sQuery(id+"F18.wireOp",VERTEX,"E155");
            var Q5;
            Q5=sQuery(id+"F18.wireOp",VERTEX,"E156");
            var Q6;
            Q6=sQuery(id+"F18.wireOp",VERTEX,"E157");
            var Q7;
            Q7=sQuery(id+"F18.wireOp",VERTEX,"E158");
            var Q8;
            Q8=sQuery(id+"F18.wireOp",VERTEX,"E260");
            var Q9;
            Q9=sQuery(id+"F18.wireOp",VERTEX,"E261");
            var Q10;
            Q10=sQuery(id+"F18.wireOp",VERTEX,"E262");
            var Q11;
            Q11=sQuery(id+"F18.wireOp",VERTEX,"E263");
            var Q12;
            Q12=sQuery(id+"F18.wireOp",VERTEX,"E162");
            var Q13;
            Q13=sQuery(id+"F18.wireOp",VERTEX,"E160");
            var Q14;
            Q14=sQuery(id+"F18.wireOp",VERTEX,"E161");
            var Q15;
            Q15=sQuery(id+"F18.wireOp",VERTEX,"E163");
            var Q16;
            Q16=sQuery(id+"F18.wireOp",VERTEX,"E167");
            var Q17;
            Q17=sQuery(id+"F18.wireOp",VERTEX,"E165");
            var Q18;
            Q18=sQuery(id+"F18.wireOp",VERTEX,"E166");
            var Q19;
            Q19=sQuery(id+"F18.wireOp",VERTEX,"E170");
            var Q20;
            Q20=sQuery(id+"F18.wireOp",VERTEX,"E171");
            var Q21;
            Q21=sQuery(id+"F18.wireOp",VERTEX,"E172");
            var Q22;
            Q22=sQuery(id+"F18.wireOp",VERTEX,"E173");
            var Q23;
            Q23=sQuery(id+"F18.wireOp",VERTEX,"E175");
            var Q24;
            Q24=sQuery(id+"F18.wireOp",VERTEX,"E176");
            var Q25;
            Q25=sQuery(id+"F18.wireOp",VERTEX,"E177");
            var Q26;
            Q26=sQuery(id+"F18.wireOp",VERTEX,"E178");
            var Q27;
            Q27=sQuery(id+"F18.wireOp",VERTEX,"E180");
            var Q28;
            Q28=sQuery(id+"F18.wireOp",VERTEX,"E181");
            var Q29;
            Q29=sQuery(id+"F18.wireOp",VERTEX,"E182");
            var Q30;
            Q30=sQuery(id+"F18.wireOp",VERTEX,"E183");
            var Q31;
            Q31=sQuery(id+"F18.wireOp",VERTEX,"E185");
            var Q32;
            Q32=sQuery(id+"F18.wireOp",VERTEX,"E186");
            var Q33;
            Q33=sQuery(id+"F18.wireOp",VERTEX,"E187");
            var Q34;
            Q34=sQuery(id+"F18.wireOp",VERTEX,"E188");
            var Q35;
            Q35=sQuery(id+"F18.wireOp",VERTEX,"E190");
            var Q36;
            Q36=sQuery(id+"F18.wireOp",VERTEX,"E191");
            var Q37;
            Q37=sQuery(id+"F18.wireOp",VERTEX,"E192");
            var Q38;
            Q38=sQuery(id+"F18.wireOp",VERTEX,"E193");
            var Q39;
            Q39=sQuery(id+"F18.wireOp",VERTEX,"E195");
            var Q40;
            Q40=sQuery(id+"F18.wireOp",VERTEX,"E197");
            var Q41;
            Q41=sQuery(id+"F18.wireOp",VERTEX,"E196");
            var Q42;
            Q42=sQuery(id+"F18.wireOp",VERTEX,"E198");
            var Q43;
            Q43=sQuery(id+"F18.wireOp",VERTEX,"E200");
            var Q44;
            Q44=sQuery(id+"F18.wireOp",VERTEX,"E202");
            var Q45;
            Q45=sQuery(id+"F18.wireOp",VERTEX,"E201");
            var Q46;
            Q46=sQuery(id+"F18.wireOp",VERTEX,"E203");
            var Q47;
            Q47=sQuery(id+"F18.wireOp",VERTEX,"E205");
            var Q48;
            Q48=sQuery(id+"F18.wireOp",VERTEX,"E207");
            var Q49;
            Q49=sQuery(id+"F18.wireOp",VERTEX,"E206");
            var Q50;
            Q50=sQuery(id+"F18.wireOp",VERTEX,"E208");
            var Q51;
            Q51=sQuery(id+"F18.wireOp",VERTEX,"E210");
            var Q52;
            Q52=sQuery(id+"F18.wireOp",VERTEX,"E212");
            var Q53;
            Q53=sQuery(id+"F18.wireOp",VERTEX,"E211");
            var Q54;
            Q54=sQuery(id+"F18.wireOp",VERTEX,"E213");
            var Q55;
            Q55=sQuery(id+"F18.wireOp",VERTEX,"E217");
            var Q56;
            Q56=sQuery(id+"F18.wireOp",VERTEX,"E215");
            var Q57;
            Q57=sQuery(id+"F18.wireOp",VERTEX,"E216");
            var Q58;
            Q58=sQuery(id+"F18.wireOp",VERTEX,"E218");
            var Q59;
            Q59=makeQuery(id+"F1.opExtrude","SWEPT_BODY",BODY,{"disambiguationData":[OSD([sQuery(id+"F0.wireOp",EDGE,"E0.bottom"),sQuery(id+"F0.wireOp",EDGE,"E0.top"),sQuery(id+"F0.wireOp",EDGE,"E0.left"),sQuery(id+"F0.wireOp",EDGE,"E0.right")])]});
            hole(context, id + "F21", {"style" : HoleStyle.SIMPLE, "endStyle" : HoleEndStyle.BLIND, "holeDiameter" : 2 * mm, "holeDepth" : 20 * mm, "locations" : qUnion([Q0, Q1, Q2, Q3, Q4, Q5, Q6, Q7, Q8, Q9, Q10, Q11, Q12, Q13, Q14, Q15, Q16, Q17, Q18, Q19, Q20, Q21, Q22, Q23, Q24, Q25, Q26, Q27, Q28, Q29, Q30, Q31, Q32, Q33, Q34, Q35, Q36, Q37, Q38, Q39, Q40, Q41, Q42, Q43, Q44, Q45, Q46, Q47, Q48, Q49, Q50, Q51, Q52, Q53, Q54, Q55, Q56, Q57, Q58]), "scope" : qUnion([Q59])});
        }
        {
            var Q0;
            Q0=makeQuery(id+"F15.boolean.opBoolean","COPY",EDGE,{"derivedFrom":makeQuery(id+"F15.opExtrude","SWEPT_EDGE",EDGE,{"disambiguationData":[OSD([sQuery(id+"F9.wireOp",EDGE,"E40.bottom"),sQuery(id+"F9.wireOp",EDGE,"E40.left")])]})});
            var Q1;
            Q1=makeQuery(id+"F15.boolean.opBoolean","COPY",EDGE,{"derivedFrom":makeQuery(id+"F15.opExtrude","SWEPT_EDGE",EDGE,{"disambiguationData":[OSD([sQuery(id+"F9.wireOp",EDGE,"E40.bottom"),sQuery(id+"F9.wireOp",EDGE,"E40.right")])]})});
            var Q2;
            Q2=makeQuery(id+"F15.boolean.opBoolean","COPY",EDGE,{"derivedFrom":makeQuery(id+"F15.opExtrude","SWEPT_EDGE",EDGE,{"disambiguationData":[OSD([sQuery(id+"F9.wireOp",EDGE,"E40.top"),sQuery(id+"F9.wireOp",EDGE,"E40.right")])]})});
            var Q3;
            Q3=makeQuery(id+"F15.boolean.opBoolean","COPY",EDGE,{"derivedFrom":makeQuery(id+"F15.opExtrude","SWEPT_EDGE",EDGE,{"disambiguationData":[OSD([sQuery(id+"F9.wireOp",EDGE,"E40.top"),sQuery(id+"F9.wireOp",EDGE,"E40.left")])]})});
            fillet(context, id + "F22", {"entities" : qUnion([Q0, Q1, Q2, Q3]), "radius" : 5 * mm, "tangentPropagation" : true, "allowEdgeOverflow" : false});
        }
    });
